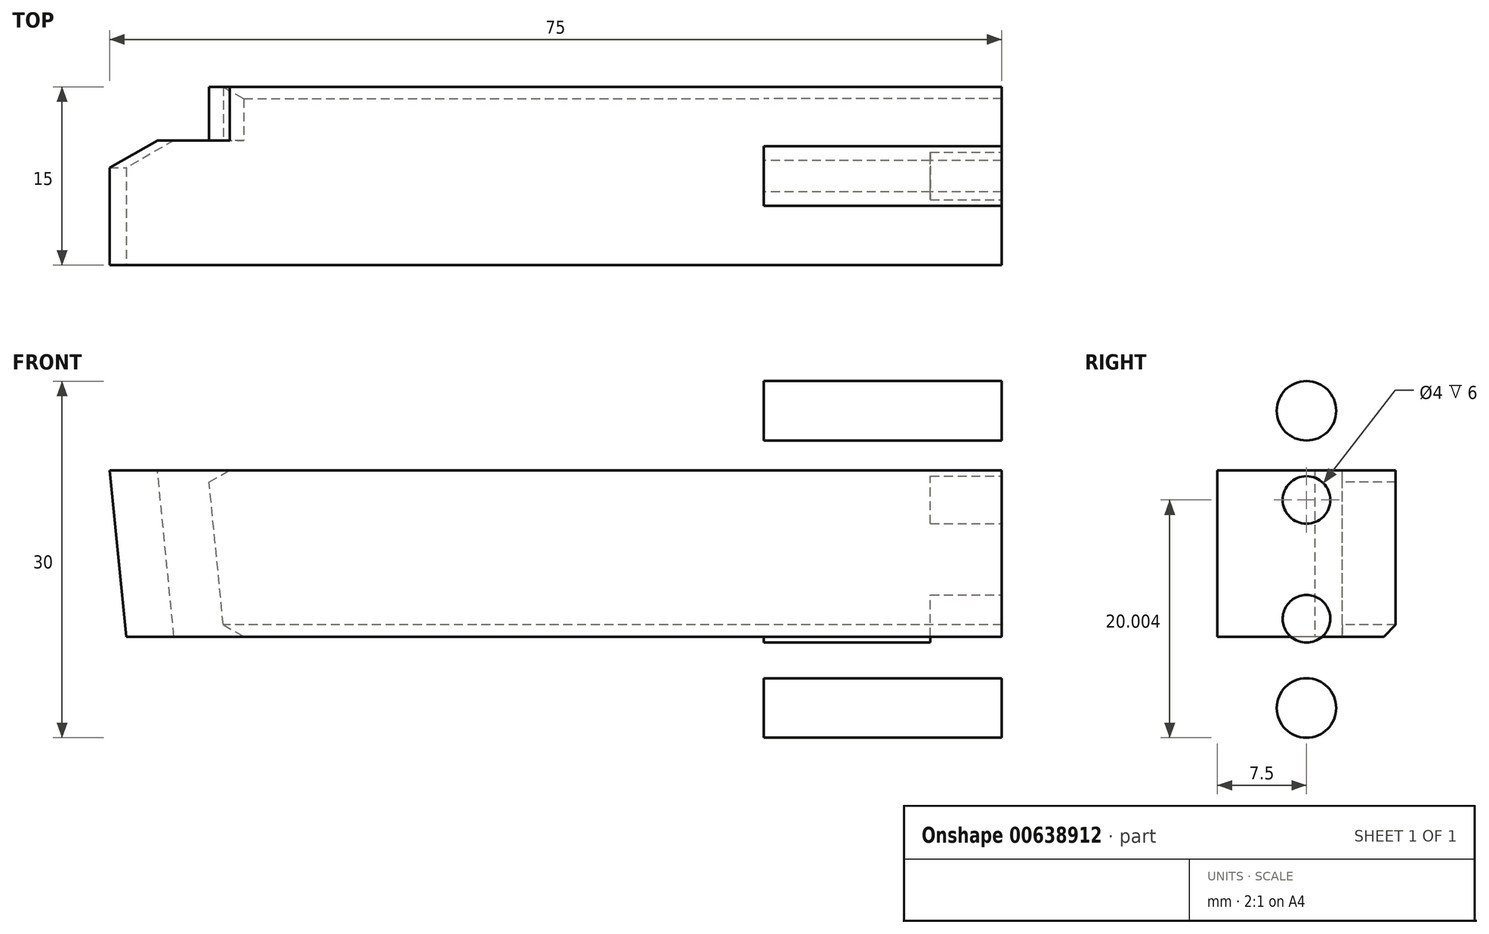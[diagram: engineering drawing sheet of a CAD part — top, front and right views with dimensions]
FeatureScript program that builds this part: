
annotation { "Feature Type Name" : "Feature", "Feature Type Description" : "" }
export const myFeature = defineFeature(function(context is Context, id is Id, definition is map)
    precondition{}
    {
        {
            var Q0;
            Q0=qCreatedBy(makeId("Front.planeOp"),FACE);
            var sketch = newSketch(context, id + "F0", { "sketchPlane" : qUnion([Q0])});
            skLineSegment(sketch, "E0", {"start": v(-74.89, -34.85) * mm, "end": v(-74.89, -69.85) * mm});
            skLineSegment(sketch, "E1", {"start": v(-74.89, -57.85) * mm, "end": v(-73.89, -58.85) * mm});
            skLineSegment(sketch, "E2", {"start": v(-74.89, -45.85) * mm, "end": v(-73.89, -44.85) * mm});
            skLineSegment(sketch, "E3", {"start": v(-74.89, -69.85) * mm, "end": v(-59.89, -69.85) * mm});
            skLineSegment(sketch, "E4", {"start": v(-73.89, -44.85) * mm, "end": v(-59.89, -44.85) * mm});
            skLineSegment(sketch, "E5", {"start": v(-74.89, -45.85) * mm, "end": v(-70.39, -45.85) * mm});
            skLineSegment(sketch, "E6", {"start": v(-74.89, -57.85) * mm, "end": v(-70.39, -57.85) * mm});
            skLineSegment(sketch, "E7", {"start": v(-73.89, -58.85) * mm, "end": v(-59.89, -58.85) * mm});
            skLineSegment(sketch, "E8", {"start": v(-70.39, -58.85) * mm, "end": v(-70.39, -44.85) * mm});
            skLineSegment(sketch, "E9", {"start": v(-68.39, -58.85) * mm, "end": v(-68.39, -44.85) * mm});
            skLineSegment(sketch, "E10", {"start": v(-59.89, -34.85) * mm, "end": v(-59.89, -69.85) * mm});
            skLineSegment(sketch, "E11", {"start": v(-74.89, -34.85) * mm, "end": v(-59.89, -34.85) * mm});
            skLineSegment(sketch, "E12", {"start": v(-67.39, -44.35) * mm, "end": v(-67.39, -35.35) * mm});
            skLineSegment(sketch, "E13", {"start": v(-71.89, -39.85) * mm, "end": v(-62.89, -39.85) * mm});
            skLineSegment(sketch, "E14", {"start": v(-67.39, -51.35) * mm, "end": v(-67.39, -43.35) * mm});
            skLineSegment(sketch, "E15", {"start": v(-71.39, -47.35) * mm, "end": v(-63.39, -47.35) * mm});
            skLineSegment(sketch, "E16", {"start": v(-67.39, -61.35) * mm, "end": v(-67.39, -53.35) * mm});
            skLineSegment(sketch, "E17", {"start": v(-71.39, -57.35) * mm, "end": v(-63.39, -57.35) * mm});
            skLineSegment(sketch, "E18", {"start": v(-67.39, -69.35) * mm, "end": v(-67.39, -60.35) * mm});
            skLineSegment(sketch, "E19", {"start": v(-71.89, -64.85) * mm, "end": v(-62.89, -64.85) * mm});
            skCircle(sketch, "E20", {"center": v(-67.39, -47.35) * mm, "radius": 2 * mm});
            skCircle(sketch, "E21", {"center": v(-67.39, -57.35) * mm, "radius": 2 * mm});
            skCircle(sketch, "E22", {"center": v(-67.39, -39.85) * mm, "radius": 2.5 * mm});
            skCircle(sketch, "E23", {"center": v(-67.39, -64.85) * mm, "radius": 2.5 * mm});
            skLineSegment(sketch, "E24", {"start": v(-59.89, 67.85) * mm, "end": v(-59.89, -7.15) * mm});
            skLineSegment(sketch, "E25", {"start": v(-74.89, 67.85) * mm, "end": v(-74.89, 1.21) * mm});
            skLineSegment(sketch, "E26", {"start": v(-59.89, 67.85) * mm, "end": v(-74.89, 67.85) * mm});
            skLineSegment(sketch, "E27", {"start": v(-59.89, 47.85) * mm, "end": v(-74.89, 47.85) * mm});
            skLineSegment(sketch, "E28", {"start": v(-59.89, -7.15) * mm, "end": v(-68.39, -7.15) * mm});
            skLineSegment(sketch, "E29", {"start": v(-70.39, -3.67) * mm, "end": v(-70.39, 1.21) * mm});
            skLineSegment(sketch, "E30", {"start": v(-74.89, 1.21) * mm, "end": v(-70.39, 1.21) * mm});
            skLineSegment(sketch, "E31", {"start": v(-68.39, -7.15) * mm, "end": v(-70.39, -3.67) * mm});
            skLineSegment(sketch, "E32", {"start": v(-73.89, 47.85) * mm, "end": v(-73.89, 2.94) * mm});
            skLineSegment(sketch, "E33", {"start": v(-70.39, 2.94) * mm, "end": v(-74.89, 2.94) * mm});
            skLineSegment(sketch, "E34", {"start": v(-70.39, 1.21) * mm, "end": v(-70.39, 2.94) * mm});
            skLineSegment(sketch, "E35", {"start": v(1.37, -44.85) * mm, "end": v(2.75, -58.85) * mm});
            skLineSegment(sketch, "E36", {"start": v(-0.73, -58.85) * mm, "end": v(-2.11, -44.85) * mm});
            skLineSegment(sketch, "E37", {"start": v(72.89, -69.85) * mm, "end": v(52.89, -69.85) * mm});
            skLineSegment(sketch, "E38", {"start": v(52.89, -58.85) * mm, "end": v(52.89, -69.85) * mm});
            skLineSegment(sketch, "E39", {"start": v(7.44, -57.85) * mm, "end": v(9.17, -58.85) * mm});
            skLineSegment(sketch, "E40", {"start": v(6.25, -45.85) * mm, "end": v(7.98, -44.85) * mm});
            skLineSegment(sketch, "E41", {"start": v(52.89, -57.85) * mm, "end": v(52.89, -58.85) * mm});
            skLineSegment(sketch, "E42", {"start": v(52.89, -44.85) * mm, "end": v(52.89, -45.85) * mm});
            skLineSegment(sketch, "E43", {"start": v(6.25, -45.85) * mm, "end": v(52.89, -45.85) * mm});
            skLineSegment(sketch, "E44", {"start": v(7.44, -57.85) * mm, "end": v(52.89, -57.85) * mm});
            skLineSegment(sketch, "E45", {"start": v(52.89, -34.85) * mm, "end": v(52.89, -44.85) * mm});
            skLineSegment(sketch, "E46", {"start": v(52.89, -34.85) * mm, "end": v(72.89, -34.85) * mm});
            skLineSegment(sketch, "E47", {"start": v(66.89, -59.35) * mm, "end": v(72.89, -59.35) * mm});
            skLineSegment(sketch, "E48", {"start": v(72.89, -55.35) * mm, "end": v(66.89, -55.35) * mm});
            skLineSegment(sketch, "E49", {"start": v(66.89, -49.35) * mm, "end": v(72.89, -49.35) * mm});
            skLineSegment(sketch, "E50", {"start": v(72.89, -45.35) * mm, "end": v(66.89, -45.35) * mm});
            skLineSegment(sketch, "E51", {"start": v(66.89, -45.35) * mm, "end": v(66.89, -49.35) * mm});
            skLineSegment(sketch, "E52", {"start": v(66.89, -49.35) * mm, "end": v(65.73, -47.35) * mm});
            skLineSegment(sketch, "E53", {"start": v(66.89, -45.35) * mm, "end": v(65.73, -47.35) * mm});
            skLineSegment(sketch, "E54", {"start": v(66.89, -55.35) * mm, "end": v(66.89, -59.35) * mm});
            skLineSegment(sketch, "E55", {"start": v(66.89, -59.35) * mm, "end": v(65.73, -57.35) * mm});
            skLineSegment(sketch, "E56", {"start": v(66.89, -55.35) * mm, "end": v(65.73, -57.35) * mm});
            skLineSegment(sketch, "E57", {"start": v(65.12, -57.35) * mm, "end": v(72.5, -57.35) * mm});
            skLineSegment(sketch, "E58", {"start": v(72.89, -69.85) * mm, "end": v(72.89, -34.85) * mm});
            skLineSegment(sketch, "E59", {"start": v(50.89, -39.85) * mm, "end": v(74.89, -39.85) * mm});
            skLineSegment(sketch, "E60", {"start": v(50.89, -64.85) * mm, "end": v(74.89, -64.85) * mm});
            skLineSegment(sketch, "E61", {"start": v(7.44, -57.85) * mm, "end": v(6.25, -45.85) * mm});
            skLineSegment(sketch, "E62", {"start": v(52.89, -58.85) * mm, "end": v(-0.73, -58.85) * mm});
            skLineSegment(sketch, "E63", {"start": v(-2.11, -44.85) * mm, "end": v(52.89, -44.85) * mm});
            skSolve(sketch);
        }
        {
            var Q0;
            {var subQ1=sQuery(id+"F0.wireOp",EDGE,"E47");Q0=makeQuery(id+"F0.imprint","IMPRINT",FACE,{"disambiguationData":[TD([[makeQuery(id+"F0.imprint","IMPRINT",EDGE,{"derivedFrom":subQ1}),1.0]])]});}
            var Q1;
            {var subQ10=sQuery(id+"F0.wireOp",EDGE,"E41");Q1=makeQuery(id+"F0.imprint","IMPRINT",FACE,{"disambiguationData":[TD([[makeQuery(id+"F0.imprint","IMPRINT",EDGE,{"derivedFrom":subQ10}),1.0]])]});}
            var Q2;
            {var subQ0=sQuery(id+"F0.wireOp",EDGE,"E49");Q2=makeQuery(id+"F0.imprint","IMPRINT",FACE,{"disambiguationData":[TD([[makeQuery(id+"F0.imprint","IMPRINT",EDGE,{"derivedFrom":subQ0}),1.0]])]});}
            var Q3;
            {var subQ0=sQuery(id+"F0.wireOp",EDGE,"E46");Q3=makeQuery(id+"F0.imprint","IMPRINT",FACE,{"disambiguationData":[TD([[makeQuery(id+"F0.imprint","IMPRINT",EDGE,{"derivedFrom":subQ0}),-1.0]])]});}
            var Q4;
            {var subQ0=sQuery(id+"F0.wireOp",EDGE,"E37");Q4=makeQuery(id+"F0.imprint","IMPRINT",FACE,{"disambiguationData":[TD([[makeQuery(id+"F0.imprint","IMPRINT",EDGE,{"derivedFrom":subQ0}),-1.0]])]});}
            var Q5;
            {var subQ0=sQuery(id+"F0.wireOp",EDGE,"E35");Q5=makeQuery(id+"F0.imprint","IMPRINT",FACE,{"disambiguationData":[TD([[makeQuery(id+"F0.imprint","IMPRINT",EDGE,{"derivedFrom":subQ0}),-1.0]])]});}
            var Q6;
            {var subQ2=sQuery(id+"F0.wireOp",EDGE,"E35");Q6=makeQuery(id+"F0.imprint","IMPRINT",FACE,{"disambiguationData":[TD([[makeQuery(id+"F0.imprint","IMPRINT",EDGE,{"derivedFrom":subQ2}),1.0]])]});}
            var Q7;
            {var subQ0=sQuery(id+"F0.wireOp",EDGE,"E40");Q7=makeQuery(id+"F0.imprint","IMPRINT",FACE,{"disambiguationData":[TD([[makeQuery(id+"F0.imprint","IMPRINT",EDGE,{"derivedFrom":subQ0}),-1.0]])]});}
            var Q8;
            {var subQ0=sQuery(id+"F0.wireOp",EDGE,"E39");Q8=makeQuery(id+"F0.imprint","IMPRINT",FACE,{"disambiguationData":[TD([[makeQuery(id+"F0.imprint","IMPRINT",EDGE,{"derivedFrom":subQ0}),1.0]])]});}
            var Q9;
            {var subQ0=sQuery(id+"F0.wireOp",EDGE,"E55");Q9=makeQuery(id+"F0.imprint","IMPRINT",FACE,{"disambiguationData":[TD([[makeQuery(id+"F0.imprint","IMPRINT",EDGE,{"derivedFrom":subQ0}),-1.0]])]});}
            var Q10;
            Q10=makeQuery(id+"F0.imprint","IMPRINT",FACE,{"disambiguationData":[TD([[makeQuery(id+"F0.imprint","IMPRINT",EDGE,{"derivedFrom":sQuery(id+"F0.wireOp",EDGE,"E51")}),-1.0]])]});
            var Q11;
            {var subQ0=sQuery(id+"F0.wireOp",EDGE,"E56");Q11=makeQuery(id+"F0.imprint","IMPRINT",FACE,{"disambiguationData":[TD([[makeQuery(id+"F0.imprint","IMPRINT",EDGE,{"derivedFrom":subQ0}),1.0]])]});}
            extrude(context, id + "F1", {"entities" : qUnion([Q0, Q1, Q2, Q3, Q4, Q5, Q6, Q7, Q8, Q9, Q10, Q11]), "oppositeDirection" : true, "depth" : 10.5 * mm, "offsetDistance" : 25 * mm});
        }
        {
            var Q0;
            Q0=makeQuery(id+"F1.opExtrude","CAP_FACE",FACE,{"disambiguationData":[OSD([sQuery(id+"F0.wireOp",EDGE,"E36"),sQuery(id+"F0.wireOp",EDGE,"E37"),sQuery(id+"F0.wireOp",EDGE,"E38"),sQuery(id+"F0.wireOp",EDGE,"E45"),sQuery(id+"F0.wireOp",EDGE,"E46"),sQuery(id+"F0.wireOp",EDGE,"E58"),sQuery(id+"F0.wireOp",EDGE,"E62"),sQuery(id+"F0.wireOp",EDGE,"E63")])],"isStart":false});
            var sketch = newSketch(context, id + "F2", { "sketchPlane" : qUnion([Q0])});
            skLineSegment(sketch, "E64.0", {"start": v(-72.89, -69.85) * mm, "end": v(-72.89, -34.85) * mm});
            skLineSegment(sketch, "E64.1", {"start": v(-72.89, -45.35) * mm, "end": v(-66.89, -45.35) * mm});
            skLineSegment(sketch, "E64.2", {"start": v(-52.89, -58.85) * mm, "end": v(-52.89, -69.85) * mm});
            skLineSegment(sketch, "E64.3", {"start": v(-66.89, -59.35) * mm, "end": v(-72.89, -59.35) * mm});
            skLineSegment(sketch, "E64.4", {"start": v(-52.89, -34.85) * mm, "end": v(-52.89, -44.85) * mm});
            skLineSegment(sketch, "E64.5", {"start": v(2.11, -44.85) * mm, "end": v(-52.89, -44.85) * mm});
            skLineSegment(sketch, "E64.6", {"start": v(-65.12, -57.35) * mm, "end": v(-72.5, -57.35) * mm});
            skLineSegment(sketch, "E64.7", {"start": v(0.73, -58.85) * mm, "end": v(2.11, -44.85) * mm});
            skLineSegment(sketch, "E64.8", {"start": v(-1.37, -44.85) * mm, "end": v(-2.75, -58.85) * mm});
            skLineSegment(sketch, "E64.9", {"start": v(-50.89, -64.85) * mm, "end": v(-74.89, -64.85) * mm});
            skLineSegment(sketch, "E64.10", {"start": v(-6.25, -45.85) * mm, "end": v(-52.89, -45.85) * mm});
            skLineSegment(sketch, "E64.11", {"start": v(-50.89, -39.85) * mm, "end": v(-74.89, -39.85) * mm});
            skLineSegment(sketch, "E64.12", {"start": v(-7.44, -57.85) * mm, "end": v(-6.25, -45.85) * mm});
            skLineSegment(sketch, "E64.13", {"start": v(-72.89, -55.35) * mm, "end": v(-66.89, -55.35) * mm});
            skLineSegment(sketch, "E64.14", {"start": v(-52.89, -58.85) * mm, "end": v(0.73, -58.85) * mm});
            skLineSegment(sketch, "E64.15", {"start": v(-52.89, -34.85) * mm, "end": v(-72.89, -34.85) * mm});
            skLineSegment(sketch, "E64.16", {"start": v(-72.89, -69.85) * mm, "end": v(-52.89, -69.85) * mm});
            skLineSegment(sketch, "E64.17", {"start": v(-66.89, -49.35) * mm, "end": v(-72.89, -49.35) * mm});
            skLineSegment(sketch, "E64.18", {"start": v(-7.44, -57.85) * mm, "end": v(-52.89, -57.85) * mm});
            skLineSegment(sketch, "E65.0", {"start": v(-6.25, -45.85) * mm, "end": v(-7.98, -44.85) * mm});
            skPoint(sketch, "E66.0", {"position": v(-8.3, -58.35) * mm});
            skLineSegment(sketch, "E67.0", {"start": v(-7.44, -57.85) * mm, "end": v(-9.17, -58.85) * mm});
            skSolve(sketch);
        }
        {
            var Q0;
            {var subQ0=sQuery(id+"F2.wireOp",EDGE,"E64.15");Q0=makeQuery(id+"F2.imprint","IMPRINT",FACE,{"disambiguationData":[TD([[makeQuery(id+"F2.imprint","IMPRINT",EDGE,{"derivedFrom":subQ0}),1.0]])]});}
            var Q1;
            Q1=makeQuery(id+"F2.imprint","IMPRINT",FACE,{"disambiguationData":[TD([[makeQuery(id+"F2.imprint","IMPRINT",EDGE,{"derivedFrom":sQuery(id+"F2.wireOp",EDGE,"E64.12")}),1.0]])]});
            var Q2;
            {var subQ0=sQuery(id+"F2.wireOp",EDGE,"E64.16");Q2=makeQuery(id+"F2.imprint","IMPRINT",FACE,{"disambiguationData":[TD([[makeQuery(id+"F2.imprint","IMPRINT",EDGE,{"derivedFrom":subQ0}),1.0]])]});}
            extrude(context, id + "F3", {"entities" : qUnion([Q0, Q1, Q2]), "operationType" : NewBodyOperationType.ADD, "depth" : 4.5 * mm, "offsetDistance" : 25 * mm});
        }
        {
            var Q0;
            Q0=makeQuery(id+"F3.boolean.opBoolean","MERGE",FACE,{"derivedFrom":[makeQuery(id+"F1.opExtrude","SWEPT_FACE",FACE,{"disambiguationData":[OSD([sQuery(id+"F0.wireOp",EDGE,"E45")])]}),makeQuery(id+"F3.opExtrude","SWEPT_FACE",FACE,{"disambiguationData":[OSD([sQuery(id+"F2.wireOp",EDGE,"E64.4")])]})]});
            var sketch = newSketch(context, id + "F4", { "sketchPlane" : qUnion([Q0])});
            skLineSegment(sketch, "E68.0", {"start": v(-15, -34.85) * mm, "end": v(-15, -44.85) * mm});
            skPoint(sketch, "E69.0", {"position": v(-7.5, -34.85) * mm});
            skLineSegment(sketch, "E70.0", {"start": v(0, -44.35) * mm, "end": v(0, -35.35) * mm});
            skLineSegment(sketch, "E71.0", {"start": v(-15, -34.85) * mm, "end": v(0, -34.85) * mm});
            skLineSegment(sketch, "E72", {"start": v(-15, -34.85) * mm, "end": v(-15, -69.85) * mm});
            skLineSegment(sketch, "E73", {"start": v(-15, -57.85) * mm, "end": v(-14, -58.85) * mm});
            skLineSegment(sketch, "E74", {"start": v(-15, -45.85) * mm, "end": v(-14, -44.85) * mm});
            skLineSegment(sketch, "E75", {"start": v(-15, -69.85) * mm, "end": v(0, -69.85) * mm});
            skLineSegment(sketch, "E76", {"start": v(-14, -44.85) * mm, "end": v(0, -44.85) * mm});
            skLineSegment(sketch, "E77", {"start": v(-15, -45.85) * mm, "end": v(-10.5, -45.85) * mm});
            skLineSegment(sketch, "E78", {"start": v(-15, -57.85) * mm, "end": v(-10.5, -57.85) * mm});
            skLineSegment(sketch, "E79", {"start": v(-14, -58.85) * mm, "end": v(0, -58.85) * mm});
            skLineSegment(sketch, "E80", {"start": v(-10.5, -58.85) * mm, "end": v(-10.5, -44.85) * mm});
            skLineSegment(sketch, "E81", {"start": v(-8.5, -58.85) * mm, "end": v(-8.5, -44.85) * mm});
            skLineSegment(sketch, "E82", {"start": v(0, -34.85) * mm, "end": v(0, -69.85) * mm});
            skCircle(sketch, "E83", {"center": v(-7.5, -47.35) * mm, "radius": 2 * mm});
            skCircle(sketch, "E84", {"center": v(-7.5, -57.35) * mm, "radius": 2 * mm});
            skCircle(sketch, "E85", {"center": v(-7.5, -39.85) * mm, "radius": 2.5 * mm});
            skCircle(sketch, "E86", {"center": v(-7.5, -64.85) * mm, "radius": 2.5 * mm});
            skSolve(sketch);
        }
        {
            var Q0;
            Q0=makeQuery(id+"F4.imprint","IMPRINT",FACE,{"disambiguationData":[TD([[makeQuery(id+"F4.imprint","IMPRINT",EDGE,{"derivedFrom":sQuery(id+"F4.wireOp",EDGE,"E85")}),-1.0]])]});
            var Q1;
            Q1=makeQuery(id+"F4.imprint","IMPRINT",FACE,{"disambiguationData":[TD([[makeQuery(id+"F4.imprint","IMPRINT",EDGE,{"derivedFrom":sQuery(id+"F4.wireOp",EDGE,"E86")}),-1.0]])]});
            extrude(context, id + "F5", {"entities" : qUnion([Q0, Q1]), "operationType" : NewBodyOperationType.REMOVE, "endBound" : BoundingType.THROUGH_ALL, "oppositeDirection" : true, "depth" : 25 * mm, "offsetDistance" : 25 * mm});
        }
        {
            var Q0;
            Q0=makeQuery(id+"F3.boolean.opBoolean","MERGE",FACE,{"derivedFrom":[makeQuery(id+"F1.opExtrude","SWEPT_FACE",FACE,{"disambiguationData":[OSD([sQuery(id+"F0.wireOp",EDGE,"E58")])]}),makeQuery(id+"F3.opExtrude","SWEPT_FACE",FACE,{"disambiguationData":[OSD([sQuery(id+"F2.wireOp",EDGE,"E64.0")])]})]});
            var sketch = newSketch(context, id + "F6", { "sketchPlane" : qUnion([Q0])});
            skCircle(sketch, "E87.0", {"center": v(7.5, -47.35) * mm, "radius": 2 * mm});
            skCircle(sketch, "E88.0", {"center": v(7.5, -57.35) * mm, "radius": 2 * mm});
            skSolve(sketch);
        }
        {
            var Q0;
            Q0=makeQuery(id+"F6.imprint","IMPRINT",FACE,{"disambiguationData":[TD([[makeQuery(id+"F6.imprint","IMPRINT",EDGE,{"derivedFrom":sQuery(id+"F6.wireOp",EDGE,"E87.0")}),1.0]])]});
            var Q1;
            Q1=makeQuery(id+"F6.imprint","IMPRINT",FACE,{"disambiguationData":[TD([[makeQuery(id+"F6.imprint","IMPRINT",EDGE,{"derivedFrom":sQuery(id+"F6.wireOp",EDGE,"E88.0")}),1.0]])]});
            extrude(context, id + "F7", {"entities" : qUnion([Q0, Q1]), "operationType" : NewBodyOperationType.REMOVE, "oppositeDirection" : true, "depth" : 6 * mm, "offsetDistance" : 25 * mm});
        }
        {
            var Q0;
            Q0=makeQuery(id+"F3.opExtrude","CAP_EDGE",EDGE,{"disambiguationData":[OSD([sQuery(id+"F2.wireOp",EDGE,"E64.5")])],"isStart":false});
            var Q1;
            Q1=makeQuery(id+"F3.opExtrude","CAP_EDGE",EDGE,{"disambiguationData":[OSD([sQuery(id+"F2.wireOp",EDGE,"E64.14")])],"isStart":false});
            chamfer(context, id + "F8", {"entities" : qUnion([Q0, Q1]), "width" : 1 * mm, "tangentPropagation" : true});
        }
        {
            var Q0;
            Q0=makeQuery(id+"F1.opExtrude","CAP_EDGE",EDGE,{"disambiguationData":[OSD([sQuery(id+"F0.wireOp",EDGE,"E36")])],"isStart":false});
            chamfer(context, id + "F9", {"entities" : qUnion([Q0]), "chamferType" : ChamferType.OFFSET_ANGLE, "width" : 4 * mm, "oppositeDirection" : false, "angle" : 30 * degree, "tangentPropagation" : true});
        }
    });
